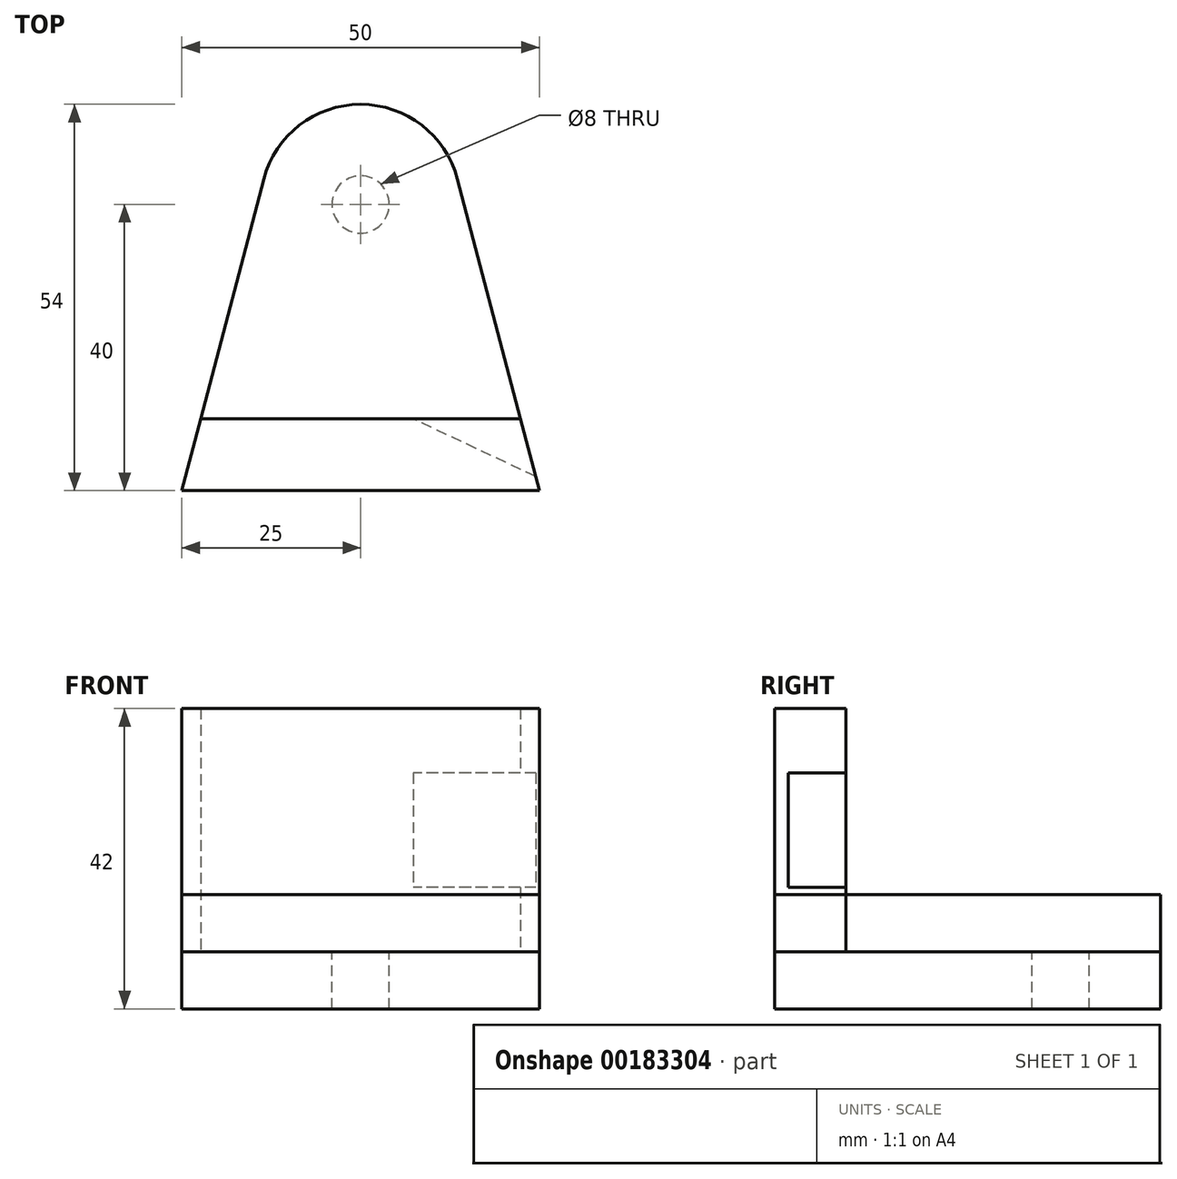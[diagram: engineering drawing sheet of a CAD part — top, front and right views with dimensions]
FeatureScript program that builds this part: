
annotation { "Feature Type Name" : "Feature", "Feature Type Description" : "" }
export const myFeature = defineFeature(function(context is Context, id is Id, definition is map)
    precondition{}
    {
        {
            var Q0;
            Q0=qCreatedBy(makeId("Top.planeOp"),FACE);
            var sketch = newSketch(context, id + "F0", { "sketchPlane" : qUnion([Q0])});
            skCircle(sketch, "E0", {"center": v(0, 0) * mm, "radius": 4 * mm});
            skArc(sketch, "E1", {"start": v(13.54, 3.56) * mm, "mid": v(0, 14) * mm, "end": v(-13.54, 3.56) * mm});
            skLineSegment(sketch, "E2.bottom", {"start": v(-14.48, 0) * mm, "end": v(-14, 0) * mm});
            skLineSegment(sketch, "E2.top", {"start": v(-25, -40) * mm, "end": v(25, -40) * mm});
            skLineSegment(sketch, "E3", {"start": v(-25, -40) * mm, "end": v(-13.54, 3.56) * mm});
            skLineSegment(sketch, "E4", {"start": v(13.54, 3.56) * mm, "end": v(25, -40) * mm});
            skPoint(sketch, "E2.left.start.orphan", {"position": v(-25, 0) * mm});
            skPoint(sketch, "E5.orphan", {"position": v(-14, 0) * mm});
            skPoint(sketch, "E6.orphan", {"position": v(14, 0) * mm});
            skLineSegment(sketch, "E7.trimOffspring", {"start": v(14, 0) * mm, "end": v(14.48, 0) * mm});
            skLineSegment(sketch, "E8.trimOffspring", {"start": v(-4, 0) * mm, "end": v(4, 0) * mm});
            skSolve(sketch);
        }
        {
            var Q0;
            Q0 = qSketchRegion(id + "F0", true);
            extrude(context, id + "F1", {"entities" : qUnion([Q0]), "oppositeDirection" : true, "depth" : 8 * mm});
        }
        {
            var Q0;
            Q0=qCreatedBy(makeId("Top.planeOp"),FACE);
            var sketch = newSketch(context, id + "F2", { "sketchPlane" : qUnion([Q0])});
            skArc(sketch, "E9", {"start": v(13.54, 3.56) * mm, "mid": v(0, 14) * mm, "end": v(-13.54, 3.56) * mm});
            skLineSegment(sketch, "E10.bottom", {"start": v(-14.48, 0) * mm, "end": v(-14, 0) * mm});
            skLineSegment(sketch, "E10.top", {"start": v(-25, -40) * mm, "end": v(25, -40) * mm});
            skLineSegment(sketch, "E11", {"start": v(-25, -40) * mm, "end": v(-13.54, 3.56) * mm});
            skLineSegment(sketch, "E12", {"start": v(13.54, 3.56) * mm, "end": v(25, -40) * mm});
            skPoint(sketch, "E10.left.start.orphan", {"position": v(-25, 0) * mm});
            skPoint(sketch, "E13.orphan", {"position": v(-14, 0) * mm});
            skPoint(sketch, "E14.orphan", {"position": v(14, 0) * mm});
            skLineSegment(sketch, "E15.trimOffspring", {"start": v(14, 0) * mm, "end": v(14.48, 0) * mm});
            skSolve(sketch);
        }
        {
            var Q0;
            Q0 = qSketchRegion(id + "F2", true);
            extrude(context, id + "F3", {"entities" : qUnion([Q0]), "depth" : 8 * mm});
        }
        {
            var Q0;
            {var subQ1=sQuery(id+"F0.wireOp",EDGE,"E1");Q0=makeQuery(id+"F0.imprint","IMPRINT",FACE,{"disambiguationData":[TD([[makeQuery(id+"F0.imprint","IMPRINT",EDGE,{"derivedFrom":subQ1}),1.0]])]});}
            var sketch = newSketch(context, id + "F4", { "sketchPlane" : qUnion([Q0])});
            skLineSegment(sketch, "E16", {"start": v(-25, -40) * mm, "end": v(-22.37, -30) * mm});
            skLineSegment(sketch, "E17", {"start": v(-22.37, -30) * mm, "end": v(22.37, -30) * mm});
            skLineSegment(sketch, "E18", {"start": v(22.37, -30) * mm, "end": v(25, -40) * mm});
            skLineSegment(sketch, "E19", {"start": v(25, -40) * mm, "end": v(-25, -40) * mm});
            skSolve(sketch);
        }
        {
            var Q0;
            Q0 = qSketchRegion(id + "F4", true);
            extrude(context, id + "F5", {"entities" : qUnion([Q0]), "depth" : 34 * mm});
        }
        {
            var Q0;
            Q0=makeQuery(id+"F5.opExtrude","SWEPT_FACE",FACE,{"disambiguationData":[OSD([sQuery(id+"F4.wireOp",EDGE,"E18")])]});
            var sketch = newSketch(context, id + "F6", { "sketchPlane" : qUnion([Q0])});
            skLineSegment(sketch, "E20.bottom", {"start": v(-43.04, 25) * mm, "end": v(-18.04, 25) * mm});
            skLineSegment(sketch, "E20.top", {"start": v(-43.04, 9) * mm, "end": v(-18.04, 9) * mm});
            skLineSegment(sketch, "E20.left", {"start": v(-43.04, 25) * mm, "end": v(-43.04, 9) * mm});
            skLineSegment(sketch, "E20.right", {"start": v(-18.04, 25) * mm, "end": v(-18.04, 9) * mm});
            skSolve(sketch);
        }
        {
            var Q0;
            {var subQ0=sQuery(id+"F6.wireOp",EDGE,"E20.right");Q0=makeQuery(id+"F6.imprint","IMPRINT",FACE,{"disambiguationData":[TD([[makeQuery(id+"F6.imprint","IMPRINT",EDGE,{"derivedFrom":subQ0}),-1.0]])]});}
            var Q1;
            {var subQ0=sQuery(id+"F6.wireOp",EDGE,"E20.left");Q1=makeQuery(id+"F6.imprint","IMPRINT",FACE,{"disambiguationData":[TD([[makeQuery(id+"F6.imprint","IMPRINT",EDGE,{"derivedFrom":subQ0}),1.0]])]});}
            var Q2;
            Q2=sQuery(id+"F6.wireOp",EDGE,"E20.left");
            revolve(context, id + "F7", {"operationType" : NewBodyOperationType.REMOVE, "entities" : qUnion([Q0, Q1]), "axis" : qUnion([Q2]), "revolveType" : RevolveType.ONE_DIRECTION, "oppositeDirection" : true, "angle" : 50 * degree});
        }
    });
